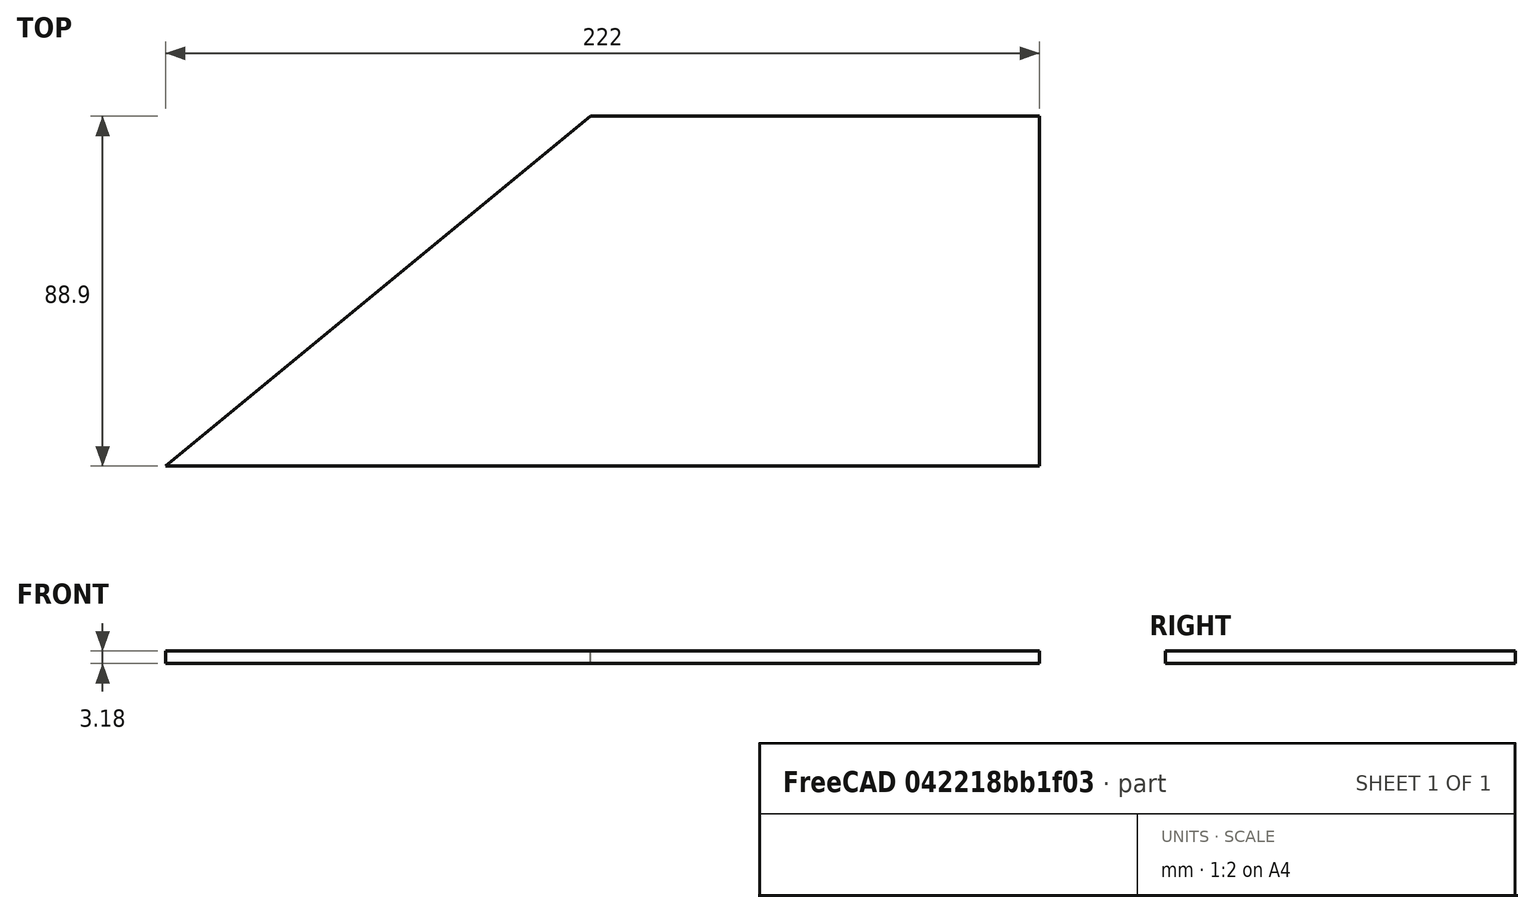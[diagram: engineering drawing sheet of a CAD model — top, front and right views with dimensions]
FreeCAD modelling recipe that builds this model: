
FCSTD DOCUMENT  (FreeCAD 1.0R39285 (Git))
Label: Fins
License: All rights reserved
LicenseURL: https://en.wikipedia.org/wiki/All_rights_reserved
objects: Sketcher::SketchObject×1, PartDesign::Pad×1, PartDesign::Body×1
note: 6 computed .brp shape members not serialized (recipe doc carries the construction recipe); baked Part::Feature solids carry a one-line shape summary decoded from their .brp

FEATURE [Sketcher::SketchObject] Sketch
  ArcFitTolerance = 1e-06
  AttachmentSupport = -> [XY_Plane]
  FullyConstrained = true
  MakeInternals = false
  MapMode = 5
  sketch-geometry (4):
    g0: LineSegment StartX=0 StartY=0 StartZ=0 EndX=222 EndY=0 EndZ=0
    g1: LineSegment StartX=222 StartY=0 StartZ=0 EndX=222 EndY=88.9 EndZ=0
    g2: LineSegment StartX=222 StartY=88.9 StartZ=0 EndX=108 EndY=88.9 EndZ=0
    g3: LineSegment StartX=108 StartY=88.9 StartZ=0 EndX=0 EndY=0 EndZ=0
  constraints (11):
    c: Distance(g0) = 222
    c: Coincident(g0,g-1)
    c: Horizontal(g0)
    c: Distance(g1) = 88.9
    c: Coincident(g1,g0)
    c: Vertical(g1)
    c: Distance(g2) = 114
    c: Coincident(g2,g1)
    c: Horizontal(g2)
    c: Coincident(g3,g2)
    c: Coincident(g3,g0)
FEATURE [PartDesign::Pad] Pad
  Direction = (0,0,1)
  Length = 3.18
  Length2 = 10
  Profile = -> Sketch
  ReferenceAxis = -> Sketch [N_Axis]
  Refine = true
  Suppressed = false
  Type = 0
FEATURE [PartDesign::Body] Body
  AllowCompound = false
  Group = -> [Sketch,Pad]
  Origin = -> Origin
  Tip = -> Pad
